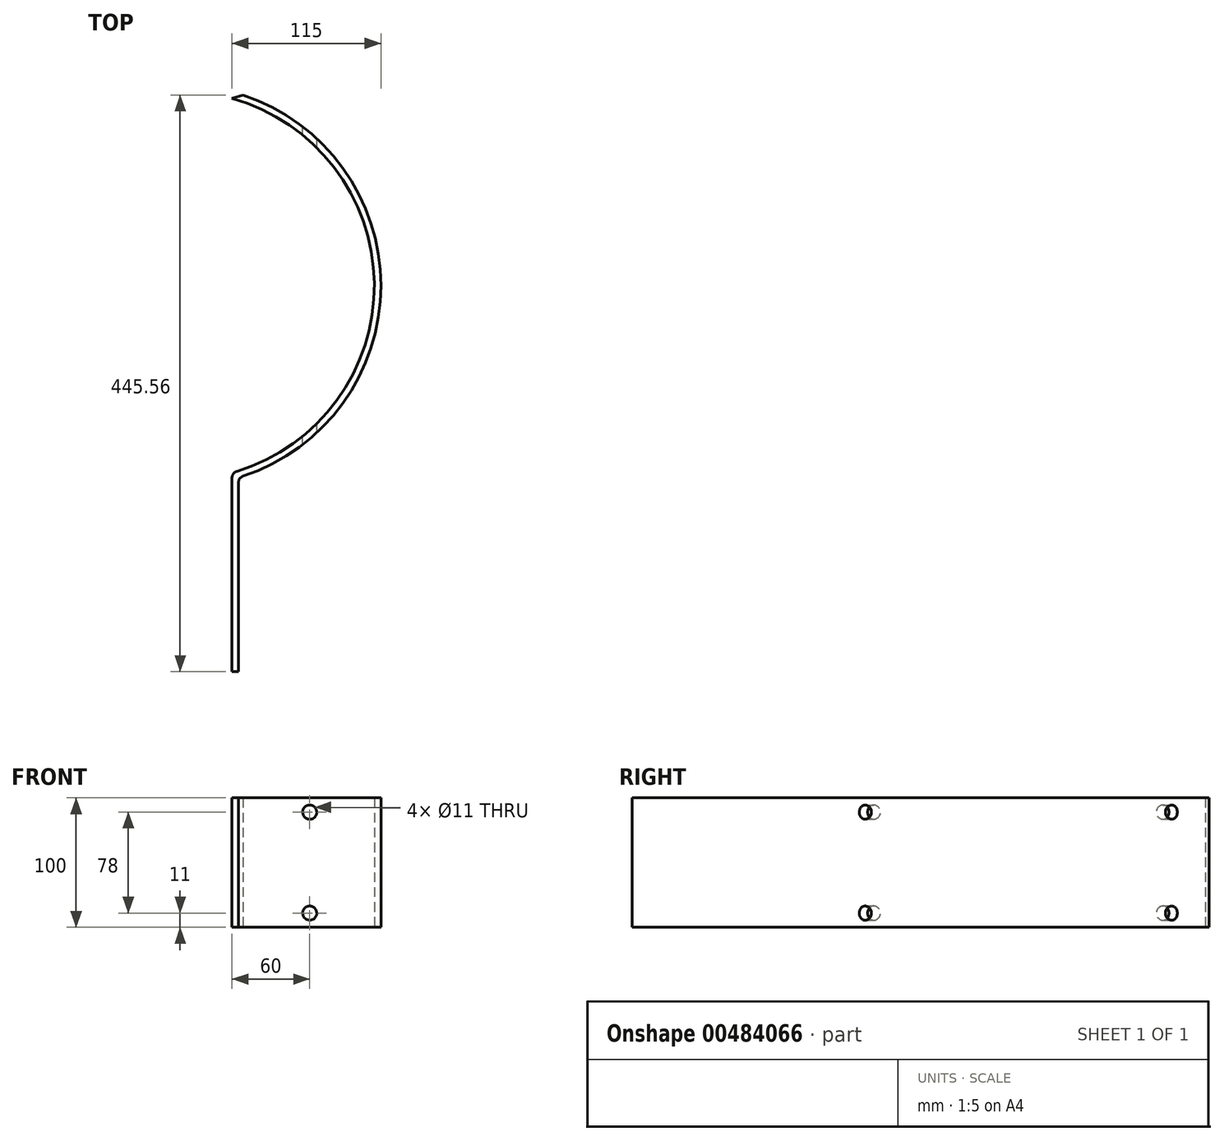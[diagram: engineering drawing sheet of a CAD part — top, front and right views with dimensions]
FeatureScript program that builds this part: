
annotation { "Feature Type Name" : "Feature", "Feature Type Description" : "" }
export const myFeature = defineFeature(function(context is Context, id is Id, definition is map)
    precondition{}
    {
        {
            var Q0;
            Q0=qCreatedBy(makeId("Top.planeOp"),FACE);
            var sketch = newSketch(context, id + "F0", { "sketchPlane" : qUnion([Q0])});
            skLineSegment(sketch, "E0", {"start": v(45, -151.99) * mm, "end": v(45, -298.32) * mm});
            skLineSegment(sketch, "E1", {"start": v(40, -298.32) * mm, "end": v(45, -298.32) * mm});
            skArc(sketch, "E2", {"start": v(43.54, -143.54) * mm, "mid": v(149.89, 1.85) * mm, "end": v(40, 144.57) * mm});
            skArc(sketch, "E3", {"start": v(48.44, -147.24) * mm, "mid": v(155, 0) * mm, "end": v(48.44, 147.24) * mm});
            skLineSegment(sketch, "E4", {"start": v(40, -148.32) * mm, "end": v(40, -298.32) * mm});
            skPoint(sketch, "E5.visualSharp", {"position": v(45, 148.32) * mm});
            skPoint(sketch, "E6.visualSharp", {"position": v(45, -148.32) * mm});
            skArc(sketch, "E6.filletArc", {"start": v(48.44, -147.24) * mm, "mid": v(45.95, -149.06) * mm, "end": v(45, -151.99) * mm});
            skPoint(sketch, "E7.visualSharp", {"position": v(40, -144.57) * mm});
            skArc(sketch, "E7.filletArc", {"start": v(43.54, -143.54) * mm, "mid": v(40.98, -145.34) * mm, "end": v(40, -148.32) * mm});
            skLineSegment(sketch, "E8", {"start": v(48.44, 147.24) * mm, "end": v(40, 144.57) * mm});
            skSolve(sketch);
        }
        {
            var Q0;
            Q0=qSketchRegion(id+"F0",true);
            extrude(context, id + "F1", {"entities" : qUnion([Q0]), "depth" : 100 * mm});
        }
        {
            var Q0;
            Q0=makeQuery(id+"F1.opExtrude","SWEPT_FACE",FACE,{"disambiguationData":[OSD([sQuery(id+"F0.wireOp",EDGE,"E1")])]});
            var sketch = newSketch(context, id + "F2", { "sketchPlane" : qUnion([Q0])});
            skLineSegment(sketch, "E9", {"start": v(45, 0) * mm, "end": v(45, 100) * mm});
            skLineSegment(sketch, "E10", {"start": v(45, 50) * mm, "end": v(100, 50) * mm});
            skLineSegment(sketch, "E11", {"start": v(100, 50) * mm, "end": v(100, 89) * mm});
            skLineSegment(sketch, "E12", {"start": v(100, 50) * mm, "end": v(100, 11) * mm});
            skSolve(sketch);
        }
        {
            var Q0;
            Q0=sQuery(id+"F2.wireOp",VERTEX,"E11.end");
            var Q1;
            Q1=sQuery(id+"F2.wireOp",VERTEX,"E12.end");
            var Q2;
            Q2=makeQuery(id+"F1.opExtrude","SWEPT_BODY",BODY,{"disambiguationData":[OSD([sQuery(id+"F0.wireOp",EDGE,"E0"),sQuery(id+"F0.wireOp",EDGE,"jm6CQQg0-pwsB-buC1-l4tw-p9Zl7HNVW6hK"),sQuery(id+"F0.wireOp",EDGE,"TLkbZRbL-qZBq-Zfl5-tVMB-57C4CQ9nFPvc"),sQuery(id+"F0.wireOp",EDGE,"E1"),sQuery(id+"F0.wireOp",EDGE,"E2"),sQuery(id+"F0.wireOp",EDGE,"E3"),sQuery(id+"F0.wireOp",EDGE,"E4"),sQuery(id+"F0.wireOp",EDGE,"u0RYlnpk-yNJg-HwwX-PstD-pkXJaXddyOqn"),sQuery(id+"F0.wireOp",EDGE,"E5.filletArc"),sQuery(id+"F0.wireOp",EDGE,"E6.filletArc"),sQuery(id+"F0.wireOp",EDGE,"E7.filletArc")])]});
            hole(context, id + "F3", {"style" : HoleStyle.SIMPLE, "endStyle" : HoleEndStyle.THROUGH, "standardTappedOrClearance" : lookupTablePath({ "standard" : "ISO", "fit" : "Normal", "size" : "M10", "type" : "Clearance" }), "standardBlindInLast" : lookupTablePath({ "fit" : "Standard", "standard" : "ISO", "size" : "M10", "type" : "Clearance" }), "holeDiameter" : 11 * mm, "isTappedThrough" : true, "tappedDepth" : 12 * mm, "tapClearance" : 3, "locations" : qUnion([Q0, Q1]), "scope" : qUnion([Q2])});
        }
    });
